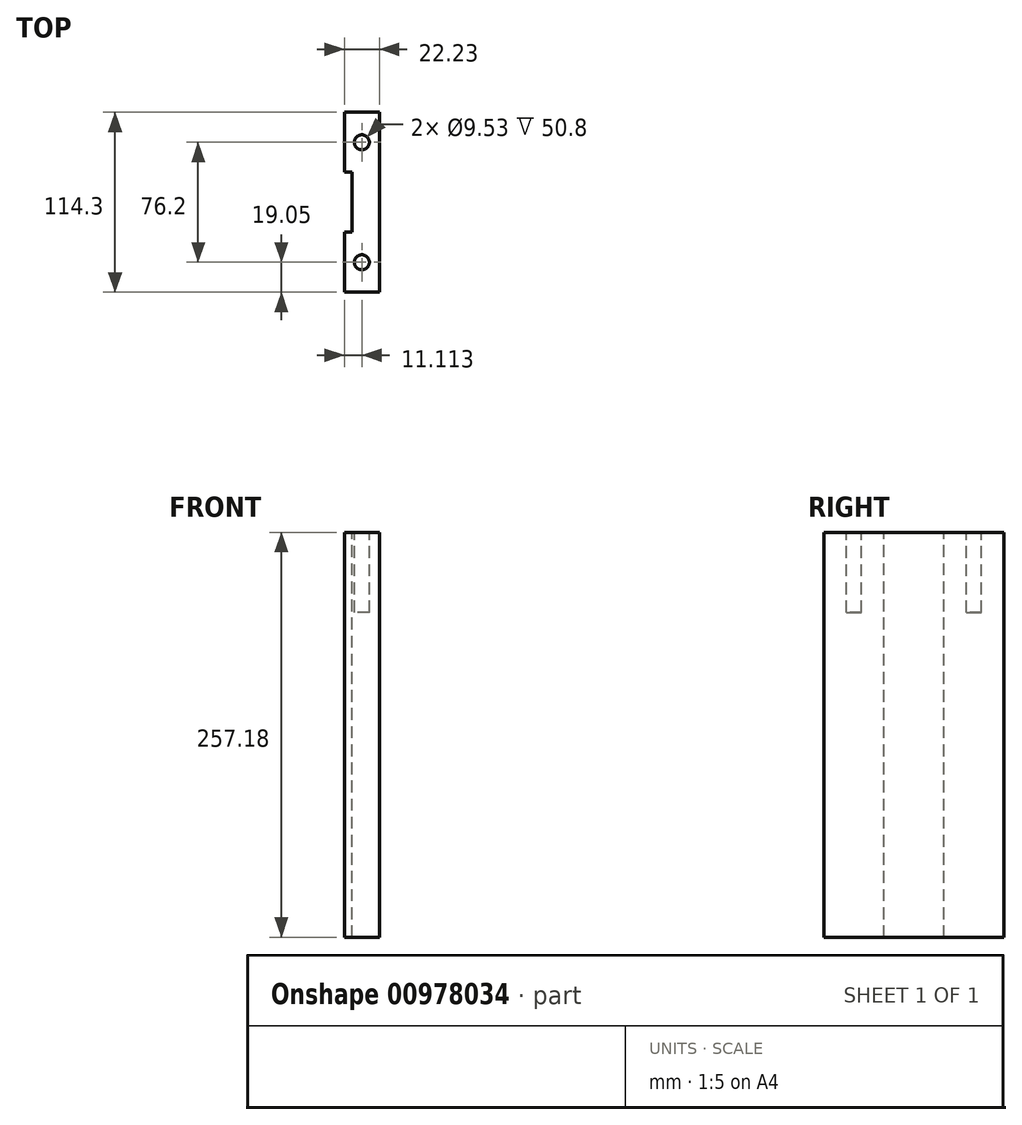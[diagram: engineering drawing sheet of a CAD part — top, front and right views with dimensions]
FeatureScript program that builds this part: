
annotation { "Feature Type Name" : "Feature", "Feature Type Description" : "" }
export const myFeature = defineFeature(function(context is Context, id is Id, definition is map)
    precondition{}
    {
        {
            var Q0;
            Q0=qCreatedBy(makeId("Right.planeOp"),FACE);
            var sketch = newSketch(context, id + "F0", { "sketchPlane" : qUnion([Q0])});
            skLineSegment(sketch, "E0", {"start": v(0, 128.59) * mm, "end": v(0, -128.59) * mm, "construction": true});
            skLineSegment(sketch, "E1", {"start": v(-57.15, 0) * mm, "end": v(57.15, 0) * mm, "construction": true});
            skLineSegment(sketch, "E2.bottom", {"start": v(-57.15, 128.59) * mm, "end": v(57.15, 128.59) * mm});
            skLineSegment(sketch, "E2.top", {"start": v(-57.15, -128.59) * mm, "end": v(57.15, -128.59) * mm});
            skLineSegment(sketch, "E2.left", {"start": v(-57.15, 128.59) * mm, "end": v(-57.15, -128.59) * mm});
            skLineSegment(sketch, "E2.right", {"start": v(57.15, 128.59) * mm, "end": v(57.15, -128.59) * mm});
            skSolve(sketch);
        }
        {
            var Q0;
            Q0=makeQuery(id+"F0.imprint","IMPRINT",FACE,{"disambiguationData":[TD([[makeQuery(id+"F0.imprint","IMPRINT",EDGE,{"derivedFrom":sQuery(id+"F0.wireOp",EDGE,"E2.bottom")}),-1.0]])]});
            extrude(context, id + "F1", {"entities" : qUnion([Q0]), "depth" : 22.22 * mm, "offsetDistance" : 25.4 * mm});
        }
        {
            var Q0;
            Q0=makeQuery(id+"F1.opExtrude","SWEPT_FACE",FACE,{"disambiguationData":[OSD([sQuery(id+"F0.wireOp",EDGE,"E2.bottom")])]});
            var sketch = newSketch(context, id + "F2", { "sketchPlane" : qUnion([Q0])});
            skLineSegment(sketch, "E3", {"start": v(0, 0) * mm, "end": v(22.23, 0) * mm, "construction": true});
            skLineSegment(sketch, "E4.0.0", {"start": v(0, 57.15) * mm, "end": v(0, -57.15) * mm});
            skLineSegment(sketch, "E4.0.1", {"start": v(0, -57.15) * mm, "end": v(22.23, -57.15) * mm});
            skLineSegment(sketch, "E4.0.2", {"start": v(22.23, -57.15) * mm, "end": v(22.23, 57.15) * mm});
            skLineSegment(sketch, "E4.0.3", {"start": v(22.23, 57.15) * mm, "end": v(0, 57.15) * mm});
            skLineSegment(sketch, "E5.bottom", {"start": v(0, -19.05) * mm, "end": v(4.76, -19.05) * mm});
            skLineSegment(sketch, "E5.top", {"start": v(0, 19.05) * mm, "end": v(4.76, 19.05) * mm});
            skLineSegment(sketch, "E5.left", {"start": v(0, -19.05) * mm, "end": v(0, 19.05) * mm});
            skLineSegment(sketch, "E5.right", {"start": v(4.76, -19.05) * mm, "end": v(4.76, 19.05) * mm});
            skSolve(sketch);
        }
        {
            var Q0;
            Q0=makeQuery(id+"F2.imprint","IMPRINT",FACE,{"disambiguationData":[TD([[makeQuery(id+"F2.imprint","IMPRINT",EDGE,{"derivedFrom":sQuery(id+"F2.wireOp",EDGE,"E5.bottom")}),1.0]])]});
            extrude(context, id + "F3", {"entities" : qUnion([Q0]), "operationType" : NewBodyOperationType.REMOVE, "endBound" : BoundingType.THROUGH_ALL, "oppositeDirection" : true, "depth" : 25.4 * mm, "offsetDistance" : 25.4 * mm});
        }
        {
            var Q0;
            Q0=makeQuery(id+"F1.opExtrude","SWEPT_FACE",FACE,{"disambiguationData":[OSD([sQuery(id+"F0.wireOp",EDGE,"E2.bottom")])]});
            var sketch = newSketch(context, id + "F4", { "sketchPlane" : qUnion([Q0])});
            skLineSegment(sketch, "E6", {"start": v(0, 0) * mm, "end": v(22.23, 0) * mm, "construction": true});
            skLineSegment(sketch, "E7", {"start": v(11.11, -57.15) * mm, "end": v(11.11, 57.15) * mm, "construction": true});
            skCircle(sketch, "E8", {"center": v(11.11, -38.1) * mm, "radius": 4.76 * mm});
            skCircle(sketch, "E9", {"center": v(11.11, 38.1) * mm, "radius": 4.76 * mm});
            skSolve(sketch);
        }
        {
            var Q0;
            Q0=makeQuery(id+"F4.imprint","IMPRINT",FACE,{"disambiguationData":[TD([[makeQuery(id+"F4.imprint","IMPRINT",EDGE,{"derivedFrom":sQuery(id+"F4.wireOp",EDGE,"E8")}),1.0]])]});
            var Q1;
            Q1=makeQuery(id+"F4.imprint","IMPRINT",FACE,{"disambiguationData":[TD([[makeQuery(id+"F4.imprint","IMPRINT",EDGE,{"derivedFrom":sQuery(id+"F4.wireOp",EDGE,"E9")}),1.0]])]});
            extrude(context, id + "F5", {"entities" : qUnion([Q0, Q1]), "operationType" : NewBodyOperationType.REMOVE, "oppositeDirection" : true, "depth" : 50.8 * mm, "offsetDistance" : 25.4 * mm});
        }
    });
